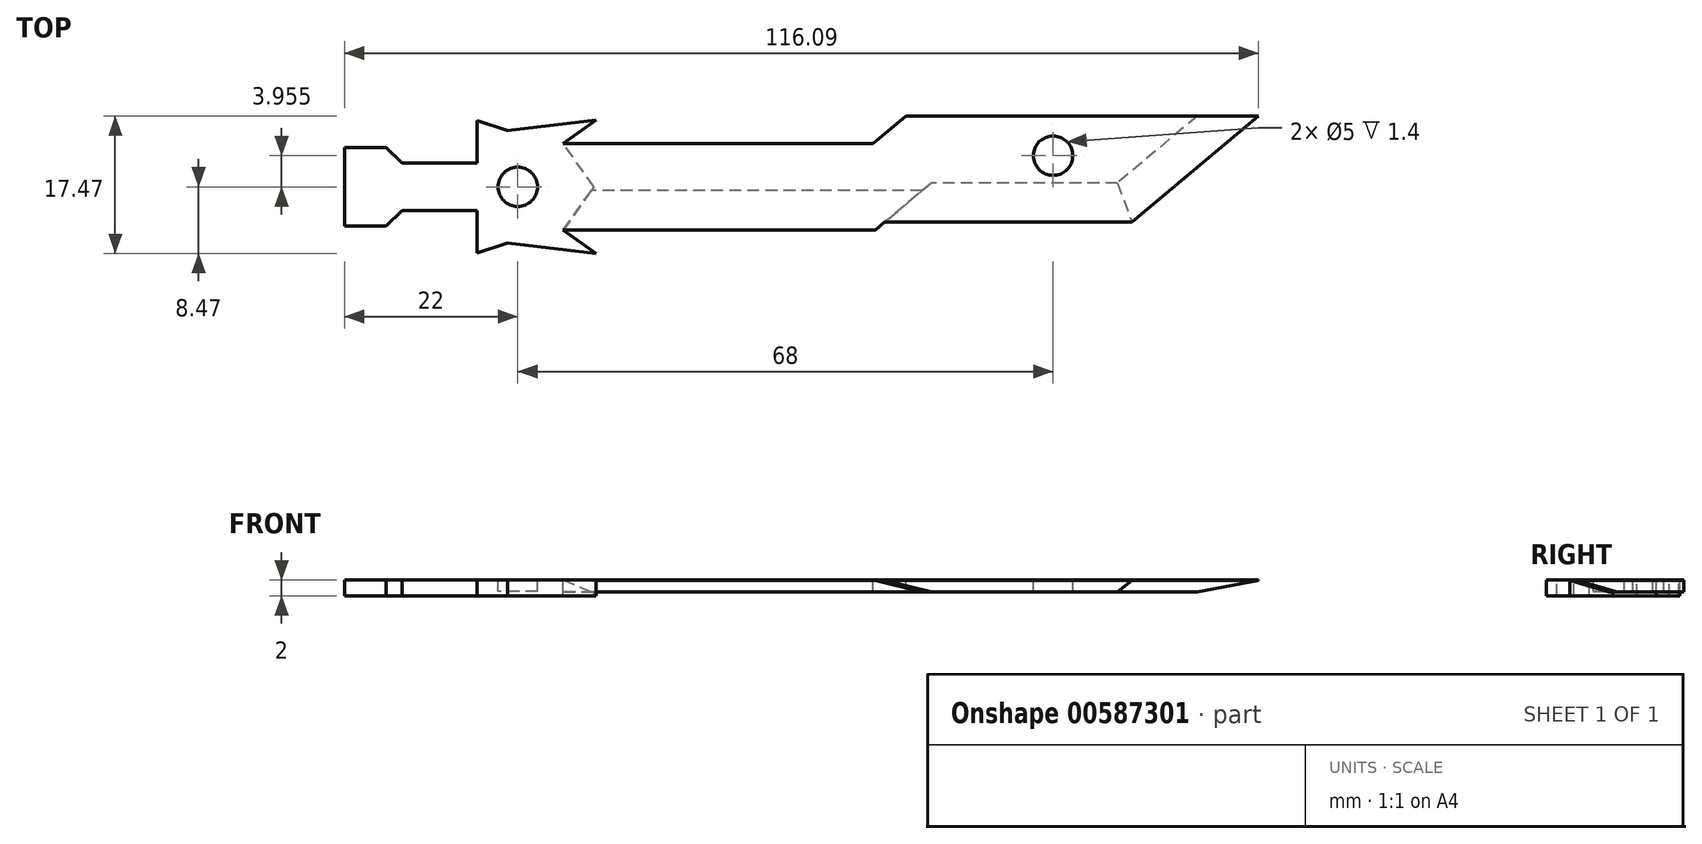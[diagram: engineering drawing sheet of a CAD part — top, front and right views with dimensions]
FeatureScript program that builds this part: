
annotation { "Feature Type Name" : "Feature", "Feature Type Description" : "" }
export const myFeature = defineFeature(function(context is Context, id is Id, definition is map)
    precondition{}
    {
        {
            var Q0;
            Q0=qCreatedBy(makeId("Top.planeOp"),FACE);
            var sketch = newSketch(context, id + "F0", { "sketchPlane" : qUnion([Q0])});
            skLineSegment(sketch, "E0", {"start": v(0, 0) * mm, "end": v(0, 5) * mm});
            skLineSegment(sketch, "E1", {"start": v(0, 5) * mm, "end": v(7.3, 5) * mm});
            skLineSegment(sketch, "E2", {"start": v(7.3, 5) * mm, "end": v(7.3, 3) * mm});
            skLineSegment(sketch, "E3", {"start": v(7.3, 3) * mm, "end": v(16.8, 3) * mm});
            skLineSegment(sketch, "E4", {"start": v(16.8, 3) * mm, "end": v(16.8, 8.39) * mm});
            skLineSegment(sketch, "E5.MirrorCS", {"start": v(7.3, -5) * mm, "end": v(7.3, -3) * mm});
            skLineSegment(sketch, "E6.MirrorCS", {"start": v(0, -5) * mm, "end": v(7.3, -5) * mm});
            skLineSegment(sketch, "E7.MirrorCS", {"start": v(7.3, -3) * mm, "end": v(16.8, -3) * mm});
            skLineSegment(sketch, "E8.MirrorCS", {"start": v(16.8, -3) * mm, "end": v(16.8, -8.39) * mm});
            skLineSegment(sketch, "E9.MirrorCS", {"start": v(0, 0) * mm, "end": v(0, -5) * mm});
            skLineSegment(sketch, "E10", {"start": v(31.96, 8.47) * mm, "end": v(27.77, 5.5) * mm});
            skLineSegment(sketch, "E11", {"start": v(27.77, 5.5) * mm, "end": v(31.67, 0) * mm});
            skLineSegment(sketch, "E12.MirrorCS", {"start": v(27.77, -5.5) * mm, "end": v(31.67, 0) * mm});
            skLineSegment(sketch, "E13.MirrorCS", {"start": v(31.96, -8.47) * mm, "end": v(27.77, -5.5) * mm});
            skLineSegment(sketch, "E14", {"start": v(31.67, 0) * mm, "end": v(31.67, 0) * mm});
            skLineSegment(sketch, "E15", {"start": v(27.77, 5.5) * mm, "end": v(67.15, 5.5) * mm});
            skLineSegment(sketch, "E16", {"start": v(27.77, -5.5) * mm, "end": v(67.4, -5.5) * mm});
            skLineSegment(sketch, "E17", {"start": v(67.15, 5.5) * mm, "end": v(71.32, 9) * mm});
            skLineSegment(sketch, "E18", {"start": v(67.4, -5.5) * mm, "end": v(68.6, -4.5) * mm});
            skLineSegment(sketch, "E19", {"start": v(71.32, 9) * mm, "end": v(116.09, 9) * mm});
            skLineSegment(sketch, "E20", {"start": v(68.6, -4.5) * mm, "end": v(100, -4.5) * mm});
            skLineSegment(sketch, "E21", {"start": v(100, -4.5) * mm, "end": v(116.09, 9) * mm});
            skLineSegment(sketch, "E22", {"start": v(16.8, -8.39) * mm, "end": v(20.67, -7.13) * mm});
            skLineSegment(sketch, "E23", {"start": v(20.67, -7.13) * mm, "end": v(31.96, -8.47) * mm});
            skLineSegment(sketch, "E24.MirrorCS", {"start": v(16.8, 8.39) * mm, "end": v(20.67, 7.13) * mm});
            skLineSegment(sketch, "E25.MirrorCS", {"start": v(20.67, 7.13) * mm, "end": v(31.96, 8.47) * mm});
            skSolve(sketch);
        }
        {
            var Q0;
            Q0=makeQuery(id+"F0.imprint","IMPRINT",FACE,{"disambiguationData":[TD([[makeQuery(id+"F0.imprint","IMPRINT",EDGE,{"derivedFrom":sQuery(id+"F0.wireOp",EDGE,"E0")}),-1.0]])]});
            extrude(context, id + "F1", {"entities" : qUnion([Q0]), "oppositeDirection" : true, "depth" : 2 * mm, "offsetDistance" : 25 * mm});
        }
        {
            var Q0;
            Q0=qSketchRegion(id+"F0",true);
            extrude(context, id + "F2", {"entities" : qUnion([Q0]), "operationType" : NewBodyOperationType.ADD, "oppositeDirection" : true, "depth" : 1.5 * mm, "offsetDistance" : 25 * mm});
        }
        {
            var Q0;
            Q0=makeQuery(id+"F2.opExtrude","CAP_EDGE",EDGE,{"disambiguationData":[OSD([sQuery(id+"F0.wireOp",EDGE,"E20")])],"isStart":false});
            chamfer(context, id + "F3", {"entities" : qUnion([Q0]), "chamferType" : ChamferType.TWO_OFFSETS, "width1" : 1.49 * mm, "oppositeDirection" : false, "width2" : 5 * mm, "tangentPropagation" : true});
        }
        {
            var Q0;
            Q0=makeQuery(id+"F2.opExtrude","CAP_EDGE",EDGE,{"disambiguationData":[OSD([sQuery(id+"F0.wireOp",EDGE,"E16")])],"isStart":false});
            chamfer(context, id + "F4", {"entities" : qUnion([Q0]), "chamferType" : ChamferType.TWO_OFFSETS, "width1" : 1.49 * mm, "oppositeDirection" : false, "width2" : 5 * mm, "tangentPropagation" : true});
        }
        {
            var Q0;
            Q0=makeQuery(id+"F2.opExtrude","CAP_EDGE",EDGE,{"disambiguationData":[OSD([sQuery(id+"F0.wireOp",EDGE,"E21")])],"isStart":false});
            chamfer(context, id + "F5", {"entities" : qUnion([Q0]), "chamferType" : ChamferType.TWO_OFFSETS, "width1" : 1.49 * mm, "oppositeDirection" : false, "width2" : 5 * mm, "tangentPropagation" : true});
        }
        {
            var Q0;
            Q0=makeQuery(id+"F1.opExtrude","SWEPT_EDGE",EDGE,{"disambiguationData":[OSD([sQuery(id+"F0.wireOp",EDGE,"E1"),sQuery(id+"F0.wireOp",EDGE,"E2")])]});
            var Q1;
            Q1=makeQuery(id+"F1.opExtrude","SWEPT_EDGE",EDGE,{"disambiguationData":[OSD([sQuery(id+"F0.wireOp",EDGE,"E5.MirrorCS"),sQuery(id+"F0.wireOp",EDGE,"E6.MirrorCS")])]});
            chamfer(context, id + "F6", {"entities" : qUnion([Q0, Q1]), "width" : 2 * mm, "tangentPropagation" : true});
        }
        {
            var Q0;
            Q0=qCreatedBy(makeId("Top.planeOp"),FACE);
            var sketch = newSketch(context, id + "F7", { "sketchPlane" : qUnion([Q0])});
            skCircle(sketch, "E26", {"center": v(22, 0) * mm, "radius": 2.5 * mm});
            skCircle(sketch, "E27", {"center": v(90, 3.95) * mm, "radius": 2.5 * mm});
            skSolve(sketch);
        }
        {
            var Q0;
            Q0=qSketchRegion(id+"F7",true);
            extrude(context, id + "F8", {"entities" : qUnion([Q0]), "operationType" : NewBodyOperationType.REMOVE, "oppositeDirection" : true, "depth" : 1.4 * mm, "offsetDistance" : 25 * mm});
        }
    });
